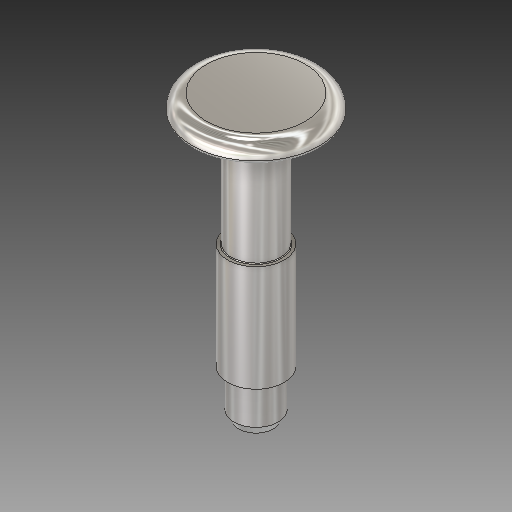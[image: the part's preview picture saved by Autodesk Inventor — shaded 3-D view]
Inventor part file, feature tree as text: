
AUTODESK INVENTOR PART (.ipt)
format: ipt  version: 2019 (Build 230136000, 136)  size: 168,448 bytes
history: native  units: in
note: dims shown in document units (in); Inventor stores cm internally (conversion verified against a paired STEP export)
features: other x3, sketch x1
ambient origin geometry x8: Origin, YZ Plane, XZ Plane, XY Plane, X Axis, Y Axis, Z Axis, Center Point
bodies: Solid1 (feature_tree)
feature tree (4):
  other  "Spring Holder Pin.ipt"
  other  "Solid1::Spring Holder Pin.ipt"
  other  "TaggingFeature1"
  sketch  "Sketch1"  dims[d0=0.3937in]
